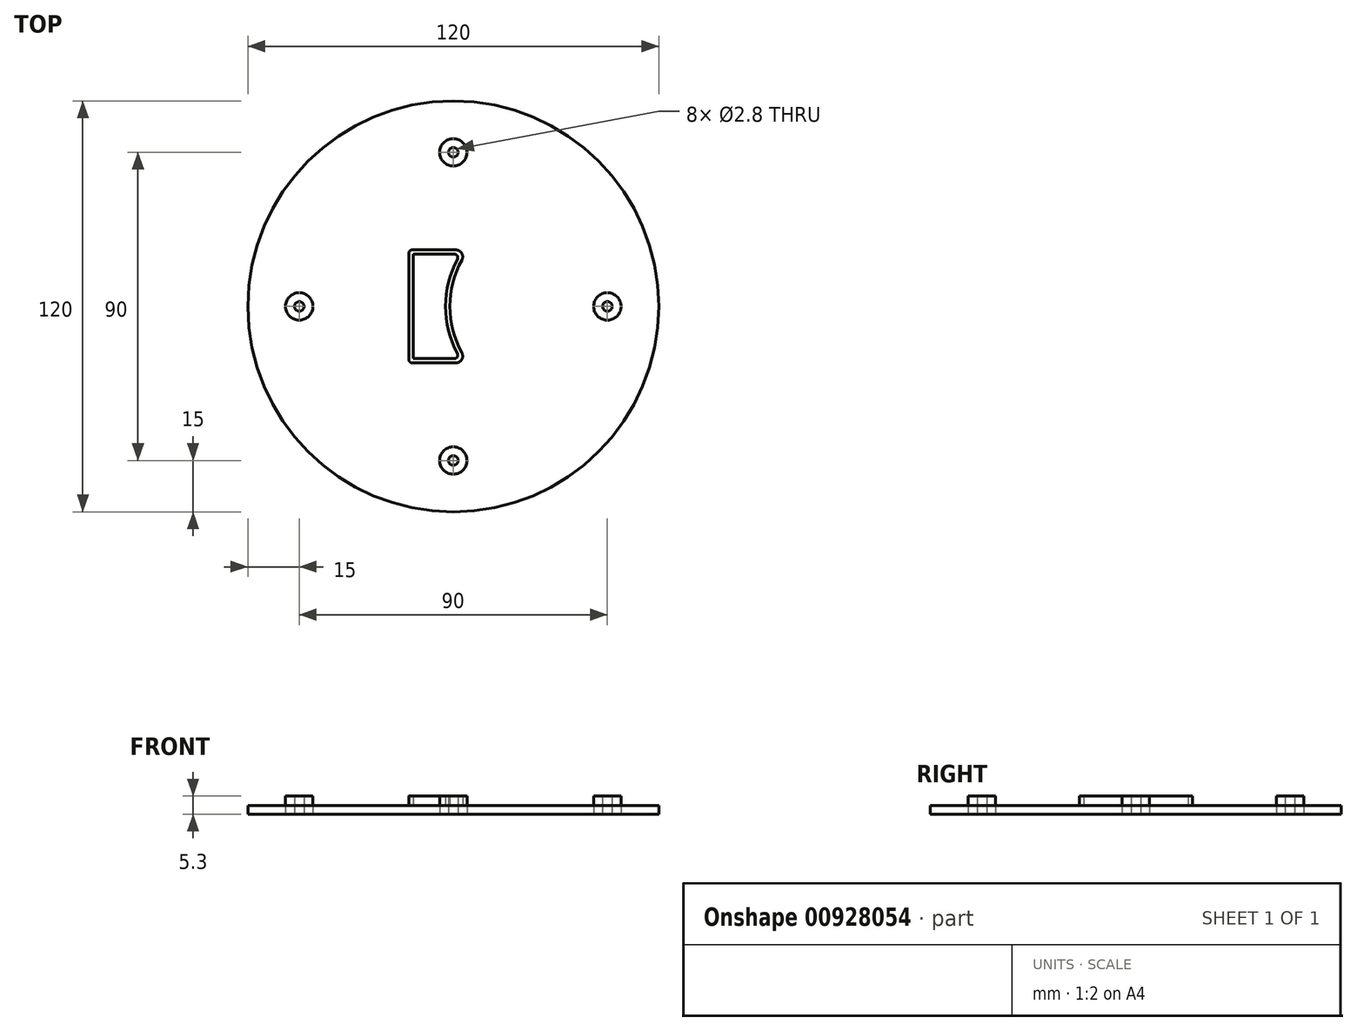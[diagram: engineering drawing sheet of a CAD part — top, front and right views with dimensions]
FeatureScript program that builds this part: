
annotation { "Feature Type Name" : "Feature", "Feature Type Description" : "" }
export const myFeature = defineFeature(function(context is Context, id is Id, definition is map)
    precondition{}
    {
        {
            var Q0;
            Q0=qCreatedBy(makeId("Top.planeOp"),FACE);
            var sketch = newSketch(context, id + "F0", { "sketchPlane" : qUnion([Q0])});
            skCircle(sketch, "E0", {"center": v(0, 0) * mm, "radius": 60 * mm});
            skSolve(sketch);
        }
        {
            var Q0;
            Q0=makeQuery(id+"F0.imprint","IMPRINT",FACE,{"disambiguationData":[TD([[makeQuery(id+"F0.imprint","IMPRINT",EDGE,{"derivedFrom":sQuery(id+"F0.wireOp",EDGE,"E0")}),1.0]])]});
            extrude(context, id + "F1", {"entities" : qUnion([Q0]), "depth" : 2.5 * mm, "offsetDistance" : 25 * mm});
        }
        {
            var Q0;
            Q0=makeQuery(id+"F1.opExtrude","CAP_FACE",FACE,{"disambiguationData":[OSD([sQuery(id+"F0.wireOp",EDGE,"E0")])],"isStart":true});
            var sketch = newSketch(context, id + "F2", { "sketchPlane" : qUnion([Q0])});
            skCircle(sketch, "E1", {"center": v(45, 0) * mm, "radius": 1.4 * mm});
            skCircle(sketch, "E2.1.0", {"center": v(0, 45) * mm, "radius": 1.4 * mm});
            skCircle(sketch, "E2.2.0", {"center": v(-45, 0) * mm, "radius": 1.4 * mm});
            skCircle(sketch, "E2.3.0", {"center": v(0, -45) * mm, "radius": 1.4 * mm});
            skPoint(sketch, "E2.center", {"position": v(0, 0) * mm});
            skCircle(sketch, "E3", {"center": v(45, 0) * mm, "radius": 4 * mm});
            skCircle(sketch, "E4.1.0", {"center": v(0, 45) * mm, "radius": 4 * mm});
            skCircle(sketch, "E4.2.0", {"center": v(-45, 0) * mm, "radius": 4 * mm});
            skCircle(sketch, "E4.3.0", {"center": v(0, -45) * mm, "radius": 4 * mm});
            skSolve(sketch);
        }
        {
            var Q0;
            Q0=makeQuery(id+"F2.imprint","IMPRINT",FACE,{"disambiguationData":[TD([[makeQuery(id+"F2.imprint","IMPRINT",EDGE,{"derivedFrom":sQuery(id+"F2.wireOp",EDGE,"E2.3.0")}),1.0]])]});
            var Q1;
            Q1=makeQuery(id+"F2.imprint","IMPRINT",FACE,{"disambiguationData":[TD([[makeQuery(id+"F2.imprint","IMPRINT",EDGE,{"derivedFrom":sQuery(id+"F2.wireOp",EDGE,"E2.2.0")}),1.0]])]});
            var Q2;
            Q2=makeQuery(id+"F2.imprint","IMPRINT",FACE,{"disambiguationData":[TD([[makeQuery(id+"F2.imprint","IMPRINT",EDGE,{"derivedFrom":sQuery(id+"F2.wireOp",EDGE,"E2.1.0")}),1.0]])]});
            var Q3;
            Q3=makeQuery(id+"F2.imprint","IMPRINT",FACE,{"disambiguationData":[TD([[makeQuery(id+"F2.imprint","IMPRINT",EDGE,{"derivedFrom":sQuery(id+"F2.wireOp",EDGE,"E1")}),1.0]])]});
            extrude(context, id + "F3", {"entities" : qUnion([Q0, Q1, Q2, Q3]), "operationType" : NewBodyOperationType.REMOVE, "endBound" : BoundingType.SYMMETRIC, "oppositeDirection" : true, "depth" : 25 * mm, "offsetDistance" : 25 * mm});
        }
        {
            var Q0;
            Q0=makeQuery(id+"F2.imprint","IMPRINT",FACE,{"disambiguationData":[TD([[makeQuery(id+"F2.imprint","IMPRINT",EDGE,{"derivedFrom":sQuery(id+"F2.wireOp",EDGE,"E2.2.0")}),-1.0]])]});
            var Q1;
            Q1=makeQuery(id+"F2.imprint","IMPRINT",FACE,{"disambiguationData":[TD([[makeQuery(id+"F2.imprint","IMPRINT",EDGE,{"derivedFrom":sQuery(id+"F2.wireOp",EDGE,"E2.3.0")}),-1.0]])]});
            var Q2;
            Q2=makeQuery(id+"F2.imprint","IMPRINT",FACE,{"disambiguationData":[TD([[makeQuery(id+"F2.imprint","IMPRINT",EDGE,{"derivedFrom":sQuery(id+"F2.wireOp",EDGE,"E1")}),-1.0]])]});
            var Q3;
            Q3=makeQuery(id+"F2.imprint","IMPRINT",FACE,{"disambiguationData":[TD([[makeQuery(id+"F2.imprint","IMPRINT",EDGE,{"derivedFrom":sQuery(id+"F2.wireOp",EDGE,"E2.1.0")}),-1.0]])]});
            var Q4;
            Q4=sQuery(id+"F2.wireOp",EDGE,"E4.3.0");
            var Q5;
            Q5=sQuery(id+"F2.wireOp",EDGE,"E3");
            var Q6;
            Q6=sQuery(id+"F2.wireOp",EDGE,"E4.1.0");
            var Q7;
            Q7=sQuery(id+"F2.wireOp",EDGE,"E4.2.0");
            extrude(context, id + "F4", {"entities" : qUnion([Q0, Q1, Q2, Q3]), "surfaceEntities" : qUnion([Q4, Q5, Q6, Q7]), "oppositeDirection" : true, "depth" : 5.3 * mm, "offsetDistance" : 25 * mm});
        }
        {
            var Q0;
            Q0=makeQuery(id+"F1.opExtrude","CAP_FACE",FACE,{"disambiguationData":[OSD([sQuery(id+"F0.wireOp",EDGE,"E0")])],"isStart":false});
            var sketch = newSketch(context, id + "F5", { "sketchPlane" : qUnion([Q0])});
            skCircle(sketch, "E5", {"center": v(27, 0) * mm, "radius": 28 * mm});
            skLineSegment(sketch, "E6.bottom", {"start": v(-13, 16.5) * mm, "end": v(7, 16.5) * mm});
            skLineSegment(sketch, "E6.top", {"start": v(-13, -16.5) * mm, "end": v(7, -16.5) * mm});
            skLineSegment(sketch, "E6.left", {"start": v(-13, 16.5) * mm, "end": v(-13, -16.5) * mm});
            skLineSegment(sketch, "E6.right", {"start": v(7, 16.5) * mm, "end": v(7, -16.5) * mm});
            skLineSegment(sketch, "E7", {"start": v(-1, 0) * mm, "end": v(-1, 33.91) * mm, "construction": true});
            skCircle(sketch, "E8", {"center": v(27, 0) * mm, "radius": 29.25 * mm});
            skLineSegment(sketch, "E9.bottom", {"start": v(-11.75, 15.25) * mm, "end": v(5.75, 15.25) * mm});
            skLineSegment(sketch, "E9.top", {"start": v(-11.75, -15.25) * mm, "end": v(5.75, -15.25) * mm});
            skLineSegment(sketch, "E9.left", {"start": v(-11.75, 15.25) * mm, "end": v(-11.75, -15.25) * mm});
            skLineSegment(sketch, "E9.right", {"start": v(5.75, 15.25) * mm, "end": v(5.75, -15.25) * mm});
            skSolve(sketch);
        }
        {
            var Q0;
            {var subQ5=sQuery(id+"F5.wireOp",EDGE,"E6.left");Q0=makeQuery(id+"F5.imprint","IMPRINT",FACE,{"disambiguationData":[TD([[makeQuery(id+"F5.imprint","IMPRINT",EDGE,{"derivedFrom":subQ5}),1.0]])]});}
            var Q1;
            {var subQ0=sQuery(id+"F5.wireOp",EDGE,"E6.bottom");var subQ1=sQuery(id+"F5.wireOp",EDGE,"E5");var subQ2=makeQuery(id+"F5.imprint","INTERSECT",VERTEX,{"derivedFrom":[subQ1,subQ0]});Q1=makeQuery(id+"F5.imprint","IMPRINT",FACE,{"disambiguationData":[TD([[makeQuery(id+"F5.imprint","IMPRINT",EDGE,{"disambiguationData":[TD([[subQ2,-1.0]])],"derivedFrom":subQ1}),-1.0]])]});}
            var Q2;
            {var subQ0=sQuery(id+"F5.wireOp",EDGE,"E9.top");var subQ1=sQuery(id+"F5.wireOp",EDGE,"E5");var subQ2=makeQuery(id+"F5.imprint","INTERSECT",VERTEX,{"derivedFrom":[subQ1,subQ0]});Q2=makeQuery(id+"F5.imprint","IMPRINT",FACE,{"disambiguationData":[TD([[makeQuery(id+"F5.imprint","IMPRINT",EDGE,{"disambiguationData":[TD([[subQ2,-1.0]])],"derivedFrom":subQ1}),-1.0]])]});}
            var Q3;
            {var subQ0=sQuery(id+"F5.wireOp",EDGE,"E9.bottom");var subQ1=sQuery(id+"F5.wireOp",EDGE,"E5");var subQ2=makeQuery(id+"F5.imprint","INTERSECT",VERTEX,{"derivedFrom":[subQ1,subQ0]});Q3=makeQuery(id+"F5.imprint","IMPRINT",FACE,{"disambiguationData":[TD([[makeQuery(id+"F5.imprint","IMPRINT",EDGE,{"disambiguationData":[TD([[subQ2,-1.0]])],"derivedFrom":subQ1}),-1.0]])]});}
            extrude(context, id + "F6", {"entities" : qUnion([Q0, Q1, Q2, Q3]), "operationType" : NewBodyOperationType.ADD, "depth" : 2.8 * mm, "offsetDistance" : 25 * mm});
        }
        {
            var Q0;
            Q0=makeQuery(id+"F6.opExtrude","SWEPT_EDGE",EDGE,{"disambiguationData":[OSD([sQuery(id+"F5.wireOp",EDGE,"E5"),sQuery(id+"F5.wireOp",EDGE,"E6.bottom")])]});
            var Q1;
            Q1=makeQuery(id+"F6.opExtrude","SWEPT_EDGE",EDGE,{"disambiguationData":[OSD([sQuery(id+"F5.wireOp",EDGE,"E5"),sQuery(id+"F5.wireOp",EDGE,"E6.top")])]});
            fillet(context, id + "F7", {"entities" : qUnion([Q0, Q1]), "radius" : 2 * mm, "tangentPropagation" : true, "allowEdgeOverflow" : false});
        }
        {
            var Q0;
            Q0=makeQuery(id+"F6.opExtrude","SWEPT_EDGE",EDGE,{"disambiguationData":[OSD([sQuery(id+"F5.wireOp",EDGE,"E8"),sQuery(id+"F5.wireOp",EDGE,"E9.top")])]});
            var Q1;
            Q1=makeQuery(id+"F6.opExtrude","SWEPT_EDGE",EDGE,{"disambiguationData":[OSD([sQuery(id+"F5.wireOp",EDGE,"E8"),sQuery(id+"F5.wireOp",EDGE,"E9.bottom")])]});
            var Q2;
            Q2=makeQuery(id+"F6.opExtrude","SWEPT_EDGE",EDGE,{"disambiguationData":[OSD([sQuery(id+"F5.wireOp",EDGE,"E6.top"),sQuery(id+"F5.wireOp",EDGE,"E6.left")])]});
            var Q3;
            Q3=makeQuery(id+"F6.opExtrude","SWEPT_EDGE",EDGE,{"disambiguationData":[OSD([sQuery(id+"F5.wireOp",EDGE,"E6.bottom"),sQuery(id+"F5.wireOp",EDGE,"E6.left")])]});
            fillet(context, id + "F8", {"entities" : qUnion([Q0, Q1, Q2, Q3]), "radius" : 1 * mm, "tangentPropagation" : true, "allowEdgeOverflow" : false});
        }
    });
